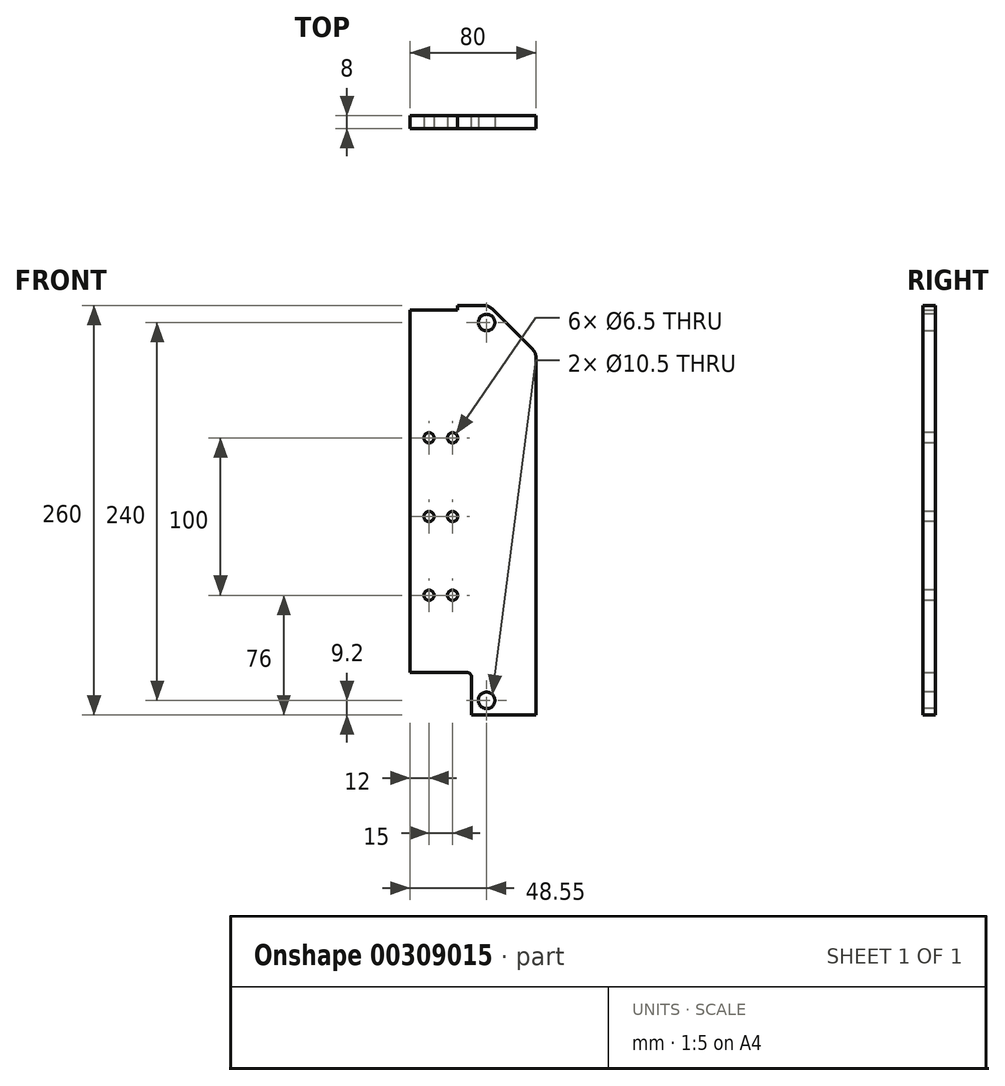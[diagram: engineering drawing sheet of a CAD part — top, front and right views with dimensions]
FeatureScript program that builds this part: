
annotation { "Feature Type Name" : "Feature", "Feature Type Description" : "" }
export const myFeature = defineFeature(function(context is Context, id is Id, definition is map)
    precondition{}
    {
        {
            var Q0;
            Q0=qCreatedBy(makeId("Front.planeOp"),FACE);
            var sketch = newSketch(context, id + "F0", { "sketchPlane" : qUnion([Q0])});
            skLineSegment(sketch, "E0", {"start": v(0, 0) * mm, "end": v(-41, 0) * mm});
            skLineSegment(sketch, "E1", {"start": v(-41, 0) * mm, "end": v(-41, 27) * mm});
            skLineSegment(sketch, "E2", {"start": v(-41, 27) * mm, "end": v(-80, 27) * mm});
            skLineSegment(sketch, "E3", {"start": v(-80, 27) * mm, "end": v(-80, 257) * mm});
            skLineSegment(sketch, "E4", {"start": v(-80, 257) * mm, "end": v(-50, 257) * mm});
            skLineSegment(sketch, "E5", {"start": v(-50, 257) * mm, "end": v(-50, 260) * mm});
            skLineSegment(sketch, "E6", {"start": v(-50, 260) * mm, "end": v(0, 260) * mm});
            skLineSegment(sketch, "E7", {"start": v(0, 260) * mm, "end": v(0, 0) * mm});
            skSolve(sketch);
        }
        {
            var Q0;
            Q0=makeQuery(id+"F0.imprint","IMPRINT",FACE,{"disambiguationData":[TD([[makeQuery(id+"F0.imprint","IMPRINT",EDGE,{"derivedFrom":sQuery(id+"F0.wireOp",EDGE,"E0")}),-1.0]])]});
            extrude(context, id + "F1", {"entities" : qUnion([Q0]), "depth" : 8 * mm});
        }
        {
            var Q0;
            Q0=makeQuery(id+"F1.opExtrude","SWEPT_EDGE",EDGE,{"disambiguationData":[OSD([sQuery(id+"F0.wireOp",EDGE,"E6"),sQuery(id+"F0.wireOp",EDGE,"E7")])]});
            chamfer(context, id + "F2", {"entities" : qUnion([Q0]), "width" : 30 * mm, "tangentPropagation" : true});
        }
        {
            var Q0;
            Q0=makeQuery(id+"F1.opExtrude","CAP_FACE",FACE,{"disambiguationData":[OSD([sQuery(id+"F0.wireOp",EDGE,"E0"),sQuery(id+"F0.wireOp",EDGE,"E1"),sQuery(id+"F0.wireOp",EDGE,"E2"),sQuery(id+"F0.wireOp",EDGE,"E3"),sQuery(id+"F0.wireOp",EDGE,"E4"),sQuery(id+"F0.wireOp",EDGE,"E5"),sQuery(id+"F0.wireOp",EDGE,"E6"),sQuery(id+"F0.wireOp",EDGE,"E7")])],"isStart":false});
            var sketch = newSketch(context, id + "F3", { "sketchPlane" : qUnion([Q0])});
            skLineSegment(sketch, "E8.bottom", {"start": v(-53, 176) * mm, "end": v(-68, 176) * mm, "construction": true});
            skLineSegment(sketch, "E8.top", {"start": v(-53, 76) * mm, "end": v(-68, 76) * mm, "construction": true});
            skLineSegment(sketch, "E8.left", {"start": v(-53, 176) * mm, "end": v(-53, 76) * mm, "construction": true});
            skLineSegment(sketch, "E8.right", {"start": v(-68, 176) * mm, "end": v(-68, 76) * mm, "construction": true});
            skPoint(sketch, "E8.middle", {"position": v(-60.5, 126) * mm});
            skLineSegment(sketch, "E9", {"start": v(-53, 126) * mm, "end": v(-68, 126) * mm, "construction": true});
            skPoint(sketch, "E10", {"position": v(-53, 176) * mm});
            skPoint(sketch, "E11", {"position": v(-68, 176) * mm});
            skPoint(sketch, "E12", {"position": v(-53, 126) * mm});
            skPoint(sketch, "E13", {"position": v(-68, 126) * mm});
            skPoint(sketch, "E14", {"position": v(-53, 76) * mm});
            skPoint(sketch, "E15", {"position": v(-68, 76) * mm});
            skSolve(sketch);
        }
        {
            var Q0;
            Q0=sQuery(id+"F3.wireOp",VERTEX,"E10");
            var Q1;
            Q1=sQuery(id+"F3.wireOp",VERTEX,"E11");
            var Q2;
            Q2=sQuery(id+"F3.wireOp",VERTEX,"E12");
            var Q3;
            Q3=sQuery(id+"F3.wireOp",VERTEX,"E13");
            var Q4;
            Q4=sQuery(id+"F3.wireOp",VERTEX,"E14");
            var Q5;
            Q5=sQuery(id+"F3.wireOp",VERTEX,"E15");
            var Q6;
            Q6=makeQuery(id+"F1.opExtrude","SWEPT_BODY",BODY,{"disambiguationData":[OSD([sQuery(id+"F0.wireOp",EDGE,"E0"),sQuery(id+"F0.wireOp",EDGE,"E1"),sQuery(id+"F0.wireOp",EDGE,"E2"),sQuery(id+"F0.wireOp",EDGE,"E3"),sQuery(id+"F0.wireOp",EDGE,"E4"),sQuery(id+"F0.wireOp",EDGE,"E5"),sQuery(id+"F0.wireOp",EDGE,"E6"),sQuery(id+"F0.wireOp",EDGE,"E7")])]});
            hole(context, id + "F4", {"style" : HoleStyle.SIMPLE, "endStyle" : HoleEndStyle.THROUGH, "holeDiameter" : 6.5 * mm, "tappedDepth" : 12 * mm, "tapClearance" : 3, "locations" : qUnion([Q0, Q1, Q2, Q3, Q4, Q5]), "scope" : qUnion([Q6])});
        }
        {
            var Q0;
            Q0=makeQuery(id+"F1.opExtrude","CAP_FACE",FACE,{"disambiguationData":[OSD([sQuery(id+"F0.wireOp",EDGE,"E0"),sQuery(id+"F0.wireOp",EDGE,"E1"),sQuery(id+"F0.wireOp",EDGE,"E2"),sQuery(id+"F0.wireOp",EDGE,"E3"),sQuery(id+"F0.wireOp",EDGE,"E4"),sQuery(id+"F0.wireOp",EDGE,"E5"),sQuery(id+"F0.wireOp",EDGE,"E6"),sQuery(id+"F0.wireOp",EDGE,"E7")])],"isStart":false});
            var sketch = newSketch(context, id + "F5", { "sketchPlane" : qUnion([Q0])});
            skLineSegment(sketch, "E16", {"start": v(-31.45, 249.2) * mm, "end": v(-31.45, 9.2) * mm, "construction": true});
            skSolve(sketch);
        }
        {
            var Q0;
            Q0=sQuery(id+"F5.wireOp",VERTEX,"E16.start");
            var Q1;
            Q1=sQuery(id+"F5.wireOp",VERTEX,"E16.end");
            var Q2;
            Q2=makeQuery(id+"F1.opExtrude","SWEPT_BODY",BODY,{"disambiguationData":[OSD([sQuery(id+"F0.wireOp",EDGE,"E0"),sQuery(id+"F0.wireOp",EDGE,"E1"),sQuery(id+"F0.wireOp",EDGE,"E2"),sQuery(id+"F0.wireOp",EDGE,"E3"),sQuery(id+"F0.wireOp",EDGE,"E4"),sQuery(id+"F0.wireOp",EDGE,"E5"),sQuery(id+"F0.wireOp",EDGE,"E6"),sQuery(id+"F0.wireOp",EDGE,"E7")])]});
            hole(context, id + "F6", {"style" : HoleStyle.SIMPLE, "endStyle" : HoleEndStyle.THROUGH, "holeDiameter" : 10.5 * mm, "tappedDepth" : 12 * mm, "tapClearance" : 3, "locations" : qUnion([Q0, Q1]), "scope" : qUnion([Q2])});
        }
        {
            var Q0;
            {var subQ0=sQuery(id+"F0.wireOp",EDGE,"E6");Q0=makeQuery(id+"F2.opChamfer","BLEND_EDGE",EDGE,{"blendedFrom":[makeQuery(id+"F1.opExtrude","SWEPT_EDGE",EDGE,{"disambiguationData":[OSD([subQ0,sQuery(id+"F0.wireOp",EDGE,"E7")])]}),makeQuery(id+"F1.opExtrude","SWEPT_FACE",FACE,{"disambiguationData":[OSD([subQ0])]})],"blendedInto":[makeQuery(id+"F1.opExtrude","SWEPT_FACE",FACE,{"disambiguationData":[OSD([subQ0])]})]});}
            var Q1;
            {var subQ0=sQuery(id+"F0.wireOp",EDGE,"E7");Q1=makeQuery(id+"F2.opChamfer","BLEND_EDGE",EDGE,{"blendedFrom":[makeQuery(id+"F1.opExtrude","SWEPT_EDGE",EDGE,{"disambiguationData":[OSD([sQuery(id+"F0.wireOp",EDGE,"E6"),subQ0])]}),makeQuery(id+"F1.opExtrude","SWEPT_FACE",FACE,{"disambiguationData":[OSD([subQ0])]})],"blendedInto":[makeQuery(id+"F1.opExtrude","SWEPT_FACE",FACE,{"disambiguationData":[OSD([subQ0])]})]});}
            fillet(context, id + "F7", {"entities" : qUnion([Q0, Q1]), "radius" : 8 * mm, "tangentPropagation" : true, "allowEdgeOverflow" : false});
        }
        {
            var Q0;
            Q0=makeQuery(id+"F1.opExtrude","SWEPT_EDGE",EDGE,{"disambiguationData":[OSD([sQuery(id+"F0.wireOp",EDGE,"E1"),sQuery(id+"F0.wireOp",EDGE,"E2")])]});
            fillet(context, id + "F8", {"entities" : qUnion([Q0]), "radius" : 3 * mm, "tangentPropagation" : true, "allowEdgeOverflow" : false});
        }
    });
